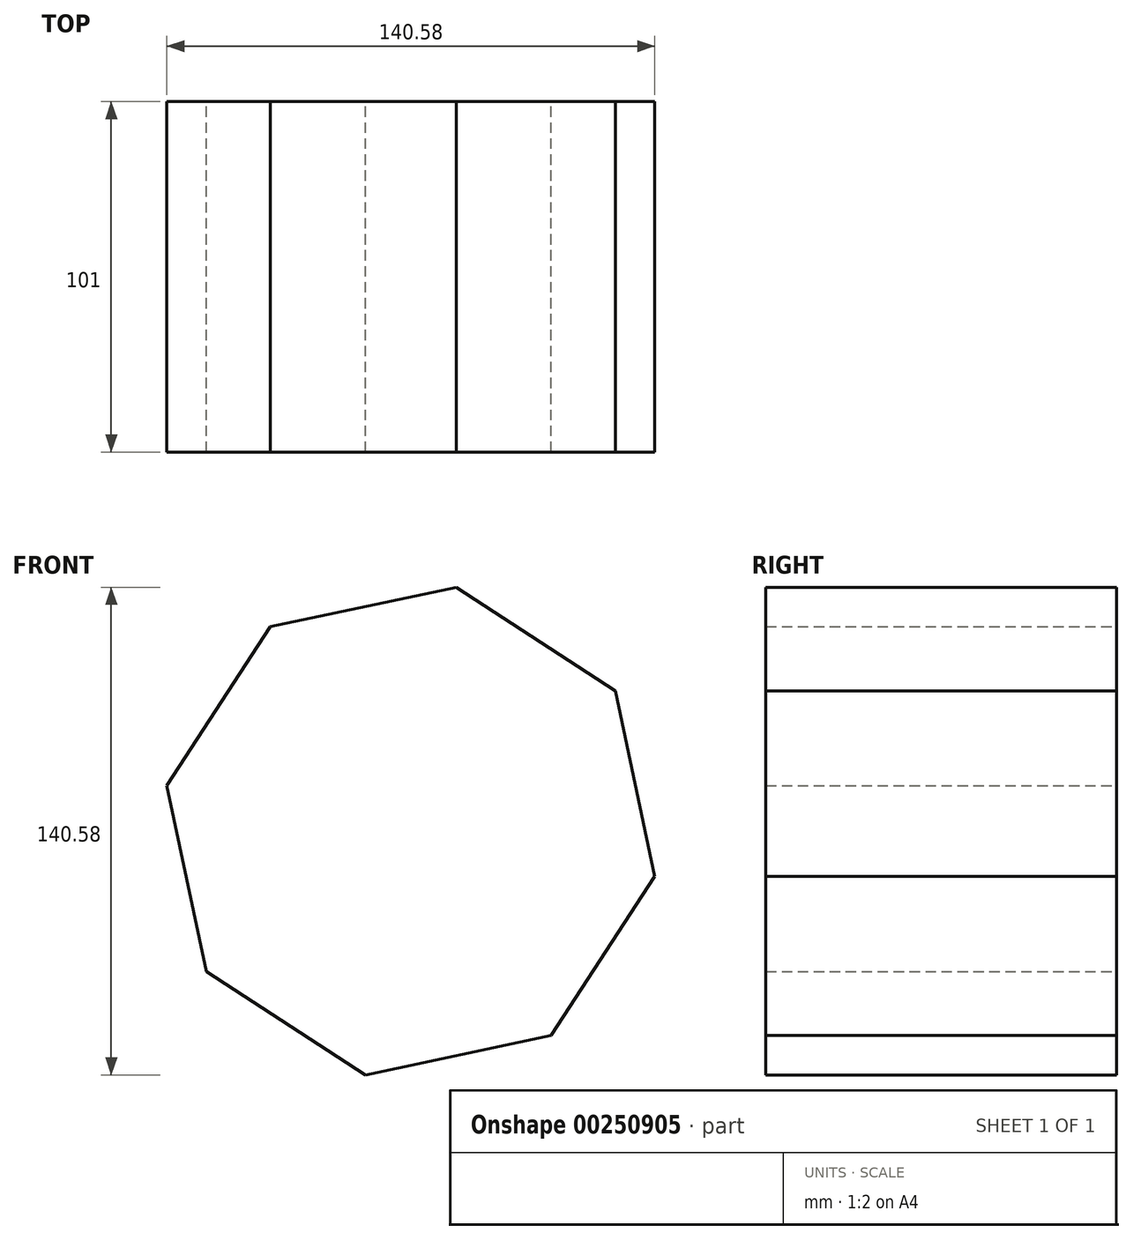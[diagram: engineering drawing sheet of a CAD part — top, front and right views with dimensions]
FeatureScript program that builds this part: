
annotation { "Feature Type Name" : "Feature", "Feature Type Description" : "" }
export const myFeature = defineFeature(function(context is Context, id is Id, definition is map)
    precondition{}
    {
        {
            var Q0;
            Q0=qCreatedBy(makeId("Front.planeOp"),FACE);
            var sketch = newSketch(context, id + "F0", { "sketchPlane" : qUnion([Q0])});
            skCircle(sketch, "E0.cCircle", {"center": v(0, 0) * mm, "radius": 71.5 * mm, "construction": true});
            skLineSegment(sketch, "E0.0", {"start": v(40.45, -58.95) * mm, "end": v(-13.08, -70.3) * mm});
            skLineSegment(sketch, "E0.1", {"start": v(-13.08, -70.3) * mm, "end": v(-58.95, -40.45) * mm});
            skLineSegment(sketch, "E0.2", {"start": v(-58.95, -40.45) * mm, "end": v(-70.3, 13.08) * mm});
            skLineSegment(sketch, "E0.3", {"start": v(-70.3, 13.08) * mm, "end": v(-40.45, 58.95) * mm});
            skLineSegment(sketch, "E0.4", {"start": v(-40.45, 58.95) * mm, "end": v(13.08, 70.3) * mm});
            skLineSegment(sketch, "E0.5", {"start": v(13.08, 70.3) * mm, "end": v(58.95, 40.45) * mm});
            skLineSegment(sketch, "E0.6", {"start": v(58.95, 40.45) * mm, "end": v(70.3, -13.08) * mm});
            skLineSegment(sketch, "E0.7", {"start": v(70.3, -13.08) * mm, "end": v(40.45, -58.95) * mm});
            skSolve(sketch);
        }
        {
            var Q0;
            Q0=makeQuery(id+"F0.imprint","IMPRINT",FACE,{"disambiguationData":[TD([[makeQuery(id+"F0.imprint","IMPRINT",EDGE,{"derivedFrom":sQuery(id+"F0.wireOp",EDGE,"E0.0")}),-1.0]])]});
            extrude(context, id + "F1", {"entities" : qUnion([Q0]), "endBound" : BoundingType.SYMMETRIC, "depth" : 101 * mm});
        }
    });
